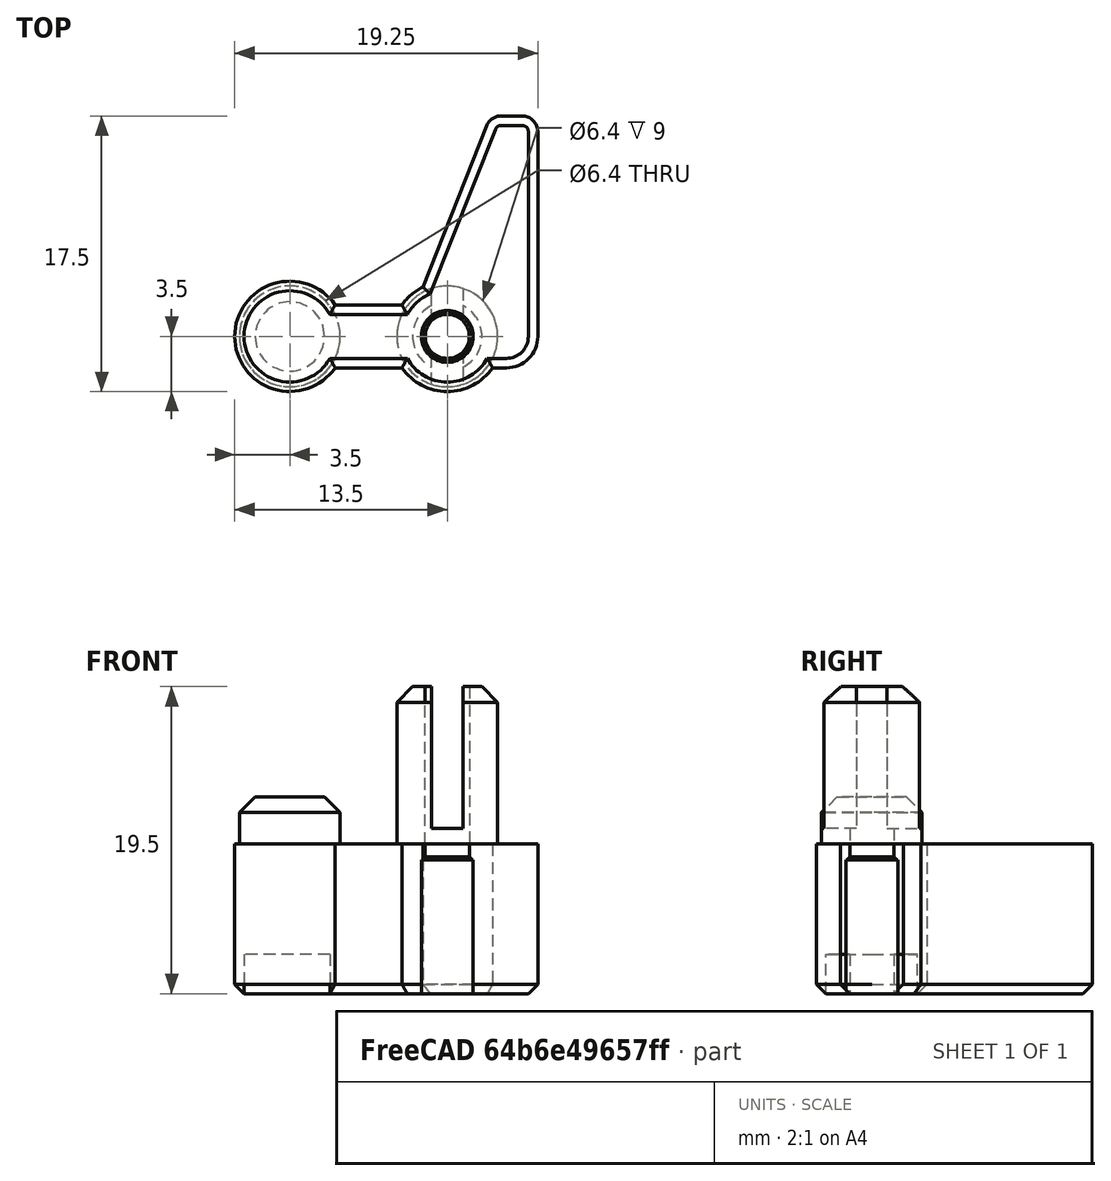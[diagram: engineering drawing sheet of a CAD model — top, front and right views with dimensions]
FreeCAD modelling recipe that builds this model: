
FCSTD DOCUMENT  (FreeCAD 0.19R24291 (Git))
Label: endstop-flag
License: All rights reserved
LicenseURL: http://en.wikipedia.org/wiki/All_rights_reserved
objects: Part::Feature×1, PartDesign::FeatureBase×1, PartDesign::Pad×1, PartDesign::Body×1
note: 5 computed .brp shape members not serialized (recipe doc carries the construction recipe); baked Part::Feature solids carry a one-line shape summary decoded from their .brp

FEATURE [Part::Feature] Chamfer005021077002006007019003032018001001  label="1x_x-endstop-flag-1515"
  shape: bbox 19.25 x 17.5 x 17 mm, 46 faces (baked)
FEATURE [PartDesign::FeatureBase] BaseFeature
  BaseFeature = -> Chamfer005021077002006007019003032018001001
FEATURE [PartDesign::Pad] Pad
  BaseFeature = -> BaseFeature
  Direction = (1,1,1)
  Length = 2.5
  Length2 = 100
  Profile = -> BaseFeature [Face8,Face29,Face9,Face28,Face27,Face26,Face25,Face24,Face22,Face21,Face23,Face20,Face6,Face3]
  Refine = true
  Type = 0
FEATURE [PartDesign::Body] Body  label="x-endtop-flag-1515-extend-2p5"
  BaseFeature = -> Chamfer005021077002006007019003032018001001
  Group = -> [BaseFeature,Pad]
  Origin = -> Origin
  Placement = pos=(0,0,0) rot=(0,1,0;3.14159rad)
  Tip = -> Pad
